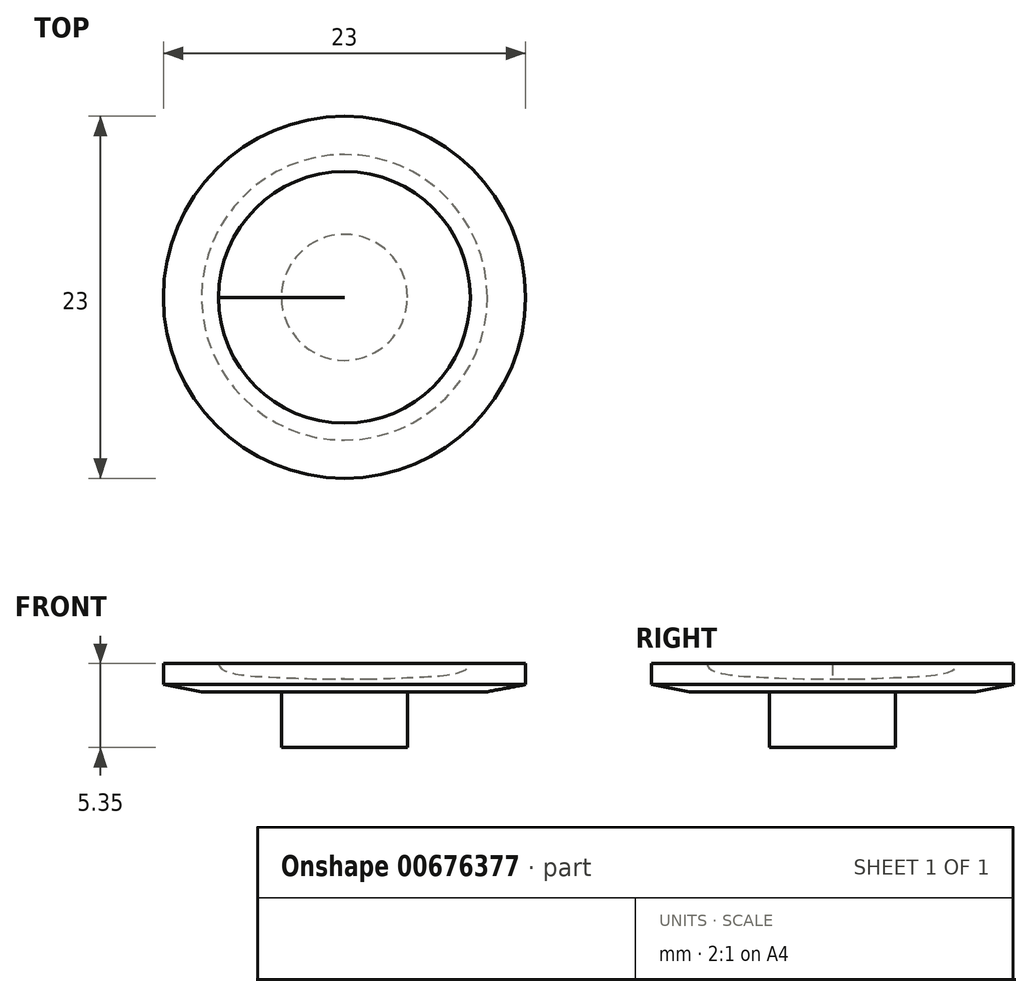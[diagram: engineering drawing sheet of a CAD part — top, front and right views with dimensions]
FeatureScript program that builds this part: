
annotation { "Feature Type Name" : "Feature", "Feature Type Description" : "" }
export const myFeature = defineFeature(function(context is Context, id is Id, definition is map)
    precondition{}
    {
        {
            var Q0;
            Q0=qCreatedBy(makeId("Front.planeOp"),FACE);
            var sketch = newSketch(context, id + "F0", { "sketchPlane" : qUnion([Q0])});
            skLineSegment(sketch, "E0", {"start": v(-11.5, 1.8) * mm, "end": v(-8, 1.8) * mm});
            skLineSegment(sketch, "E1", {"start": v(-11.5, 1.8) * mm, "end": v(-11.5, 0.45) * mm});
            skLineSegment(sketch, "E2", {"start": v(-9.07, 0) * mm, "end": v(0, 0) * mm});
            skLineSegment(sketch, "E3", {"start": v(-11.5, 0.45) * mm, "end": v(-9.07, 0) * mm});
            skFitSpline(sketch, "E4", {"points": [v(-8, 1.8) * mm, v(-4.15, 0.9) * mm, v(0, 0.85) * mm], "startDerivative": vector(0, -4.6) * mm, "endDerivative": vector(8.52, 0.54) * mm});
            skLineSegment(sketch, "E5", {"start": v(0, 0) * mm, "end": v(0, 0.85) * mm});
            skLineSegment(sketch, "E6", {"start": v(0, 2.4) * mm, "end": v(0, 0) * mm, "construction": true});
            skSolve(sketch);
        }
        {
            var Q0;
            Q0=qSketchRegion(id+"F0",true);
            var Q1;
            Q1=sQuery(id+"F0.wireOp",EDGE,"E6");
            revolve(context, id + "F1", {"entities" : qUnion([Q0]), "axis" : qUnion([Q1]), "revolveType" : RevolveType.FULL});
        }
        {
            var Q0;
            Q0=makeQuery(id+"F1.opRevolve","SWEPT_FACE",FACE,{"disambiguationData":[OSD([sQuery(id+"F0.wireOp",EDGE,"E2")])]});
            var sketch = newSketch(context, id + "F2", { "sketchPlane" : qUnion([Q0])});
            skCircle(sketch, "E7", {"center": v(0, 0) * mm, "radius": 4 * mm});
            skSolve(sketch);
        }
        {
            var Q0;
            Q0=makeQuery(id+"F2.imprint","IMPRINT",FACE,{"disambiguationData":[TD([[makeQuery(id+"F2.imprint","IMPRINT",EDGE,{"derivedFrom":sQuery(id+"F2.wireOp",EDGE,"E7")}),1.0]])]});
            extrude(context, id + "F3", {"entities" : qUnion([Q0]), "operationType" : NewBodyOperationType.ADD, "depth" : 3.55 * mm, "offsetDistance" : 25 * mm});
        }
    });
